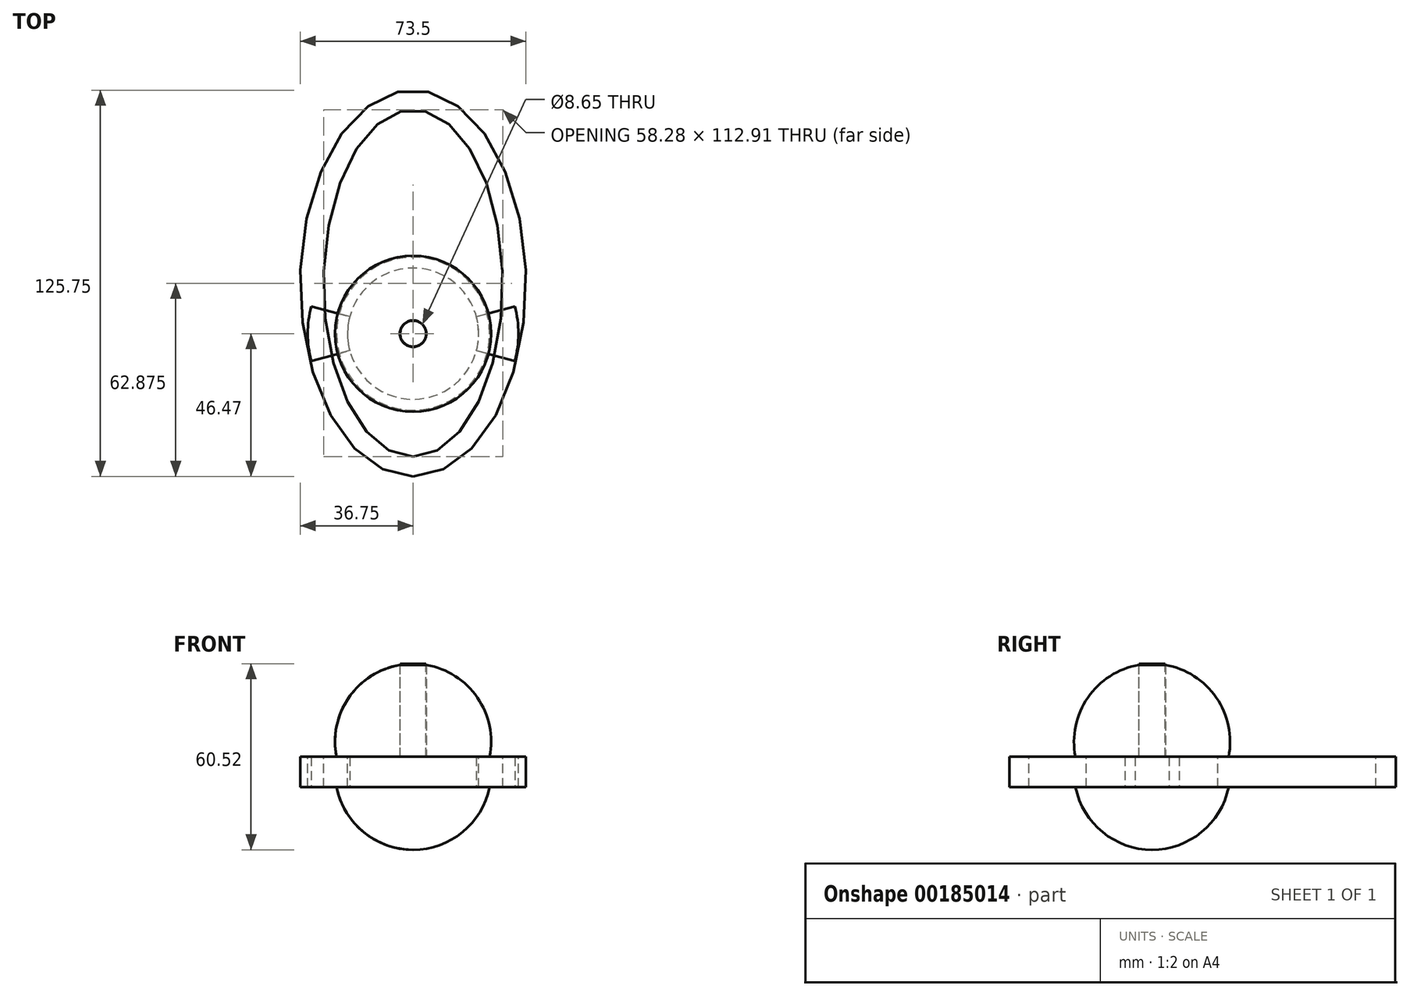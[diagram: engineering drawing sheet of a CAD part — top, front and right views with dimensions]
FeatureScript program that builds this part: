
annotation { "Feature Type Name" : "Feature", "Feature Type Description" : "" }
export const myFeature = defineFeature(function(context is Context, id is Id, definition is map)
    precondition{}
    {
        {
            var Q0;
            Q0=qCreatedBy(makeId("Front.planeOp"),FACE);
            var sketch = newSketch(context, id + "F0", { "sketchPlane" : qUnion([Q0])});
            skLineSegment(sketch, "E0", {"start": v(0, 0) * mm, "end": v(4.22, 0) * mm});
            skLineSegment(sketch, "E1", {"start": v(4.22, 0) * mm, "end": v(4.22, 30.26) * mm});
            skLineSegment(sketch, "E2", {"start": v(0, 0) * mm, "end": v(0, 7.45) * mm});
            skLineSegment(sketch, "E3", {"start": v(0, 56.49) * mm, "end": v(0, 30.26) * mm, "construction": true});
            skLineSegment(sketch, "E4", {"start": v(0, -25.4) * mm, "end": v(0, 0) * mm});
            skLineSegment(sketch, "E5", {"start": v(4.22, 30.26) * mm, "end": v(0, 30.26) * mm});
            skLineSegment(sketch, "E6", {"start": v(0, 30.26) * mm, "end": v(0, 7.45) * mm});
            skLineSegment(sketch, "E7.trimOffspring", {"start": v(0, 0) * mm, "end": v(0, -51.13) * mm, "construction": true});
            skLineSegment(sketch, "E8", {"start": v(0, 0) * mm, "end": v(21.35, 0) * mm});
            skPoint(sketch, "E8.endSnap0", {"position": v(2.1, 0) * mm});
            skLineSegment(sketch, "E9", {"start": v(21.35, 0) * mm, "end": v(21.35, -9.9) * mm});
            skLineSegment(sketch, "E10", {"start": v(21.35, -9.9) * mm, "end": v(0, -9.9) * mm});
            skSolve(sketch);
        }
        {
            var Q0;
            Q0=qCreatedBy(makeId("Front.planeOp"),FACE);
            var sketch = newSketch(context, id + "F1", { "sketchPlane" : qUnion([Q0])});
            skLineSegment(sketch, "E11", {"start": v(0, 0) * mm, "end": v(34.3, 0) * mm});
            skLineSegment(sketch, "E12", {"start": v(34.3, 0) * mm, "end": v(43.18, 0) * mm});
            skLineSegment(sketch, "E13", {"start": v(43.18, 0) * mm, "end": v(43.18, -9.9) * mm});
            skLineSegment(sketch, "E14", {"start": v(43.18, -9.9) * mm, "end": v(0, -9.9) * mm});
            skLineSegment(sketch, "E15", {"start": v(0, 0) * mm, "end": v(0, -9.9) * mm});
            skLineSegment(sketch, "E16", {"start": v(0, -9.9) * mm, "end": v(-43.18, -9.9) * mm});
            skLineSegment(sketch, "E17", {"start": v(-43.18, -9.9) * mm, "end": v(-43.18, 0) * mm});
            skLineSegment(sketch, "E18", {"start": v(-43.18, 0) * mm, "end": v(0, 0) * mm});
            skLineSegment(sketch, "E19", {"start": v(34.3, 0) * mm, "end": v(34.3, -9.9) * mm});
            skLineSegment(sketch, "E20", {"start": v(0, 0) * mm, "end": v(-34.3, 0) * mm});
            skLineSegment(sketch, "E21", {"start": v(-34.3, 0) * mm, "end": v(-34.3, -9.9) * mm});
            skLineSegment(sketch, "E22", {"start": v(0, 0) * mm, "end": v(21.35, 0) * mm});
            skLineSegment(sketch, "E23", {"start": v(0, 0) * mm, "end": v(-21.35, 0) * mm});
            skLineSegment(sketch, "E24", {"start": v(-21.35, 0) * mm, "end": v(-21.35, -9.9) * mm});
            skLineSegment(sketch, "E25", {"start": v(21.35, 0) * mm, "end": v(21.35, -9.9) * mm});
            skLineSegment(sketch, "E26", {"start": v(21.35, 0) * mm, "end": v(21.35, -1.77) * mm});
            skLineSegment(sketch, "E27", {"start": v(21.35, -9.9) * mm, "end": v(21.35, -8.12) * mm});
            skLineSegment(sketch, "E28", {"start": v(21.35, -8.12) * mm, "end": v(43.18, -8.12) * mm});
            skLineSegment(sketch, "E29", {"start": v(21.35, -1.77) * mm, "end": v(43.18, -1.77) * mm});
            skLineSegment(sketch, "E30", {"start": v(-21.35, -9.9) * mm, "end": v(-21.35, -8.12) * mm});
            skLineSegment(sketch, "E31", {"start": v(-21.35, 0) * mm, "end": v(-21.35, -1.77) * mm});
            skLineSegment(sketch, "E32", {"start": v(-21.35, -1.77) * mm, "end": v(-43.18, -1.77) * mm});
            skLineSegment(sketch, "E33", {"start": v(-21.35, -8.12) * mm, "end": v(-43.18, -8.12) * mm});
            skSolve(sketch);
        }
        {
            var Q0;
            {var subQ5=sQuery(id+"F1.wireOp",EDGE,"E24");Q0=makeQuery(id+"F1.imprint","IMPRINT",FACE,{"disambiguationData":[TD([[makeQuery(id+"F1.imprint","IMPRINT",EDGE,{"derivedFrom":subQ5}),-1.0]])]});}
            var Q1;
            {var subQ5=sQuery(id+"F1.wireOp",EDGE,"E25");Q1=makeQuery(id+"F1.imprint","IMPRINT",FACE,{"disambiguationData":[TD([[makeQuery(id+"F1.imprint","IMPRINT",EDGE,{"derivedFrom":subQ5}),1.0]])]});}
            var Q2;
            {var subQ0=sQuery(id+"F1.wireOp",EDGE,"E20");Q2=makeQuery(id+"F1.imprint","IMPRINT",FACE,{"disambiguationData":[TD([[makeQuery(id+"F1.imprint","IMPRINT",EDGE,{"derivedFrom":subQ0}),1.0]])]});}
            var Q3;
            {var subQ3=sQuery(id+"F1.wireOp",EDGE,"E30");Q3=makeQuery(id+"F1.imprint","IMPRINT",FACE,{"disambiguationData":[TD([[makeQuery(id+"F1.imprint","IMPRINT",EDGE,{"derivedFrom":subQ3}),1.0]])]});}
            var Q4;
            {var subQ3=sQuery(id+"F1.wireOp",EDGE,"E27");Q4=makeQuery(id+"F1.imprint","IMPRINT",FACE,{"disambiguationData":[TD([[makeQuery(id+"F1.imprint","IMPRINT",EDGE,{"derivedFrom":subQ3}),-1.0]])]});}
            var Q5;
            {var subQ0=sQuery(id+"F1.wireOp",EDGE,"E11");Q5=makeQuery(id+"F1.imprint","IMPRINT",FACE,{"disambiguationData":[TD([[makeQuery(id+"F1.imprint","IMPRINT",EDGE,{"derivedFrom":subQ0}),-1.0]])]});}
            var Q6;
            Q6=sQuery(id+"F0.wireOp",EDGE,"E3");
            revolve(context, id + "F2", {"entities" : qUnion([Q0, Q1, Q2, Q3, Q4, Q5]), "axis" : qUnion([Q6]), "revolveType" : RevolveType.SYMMETRIC, "angle" : 30 * degree});
        }
        {
            var Q0;
            Q0=qSketchRegion(id+"F0",true);
            var Q1;
            Q1=sQuery(id+"F0.wireOp",EDGE,"E3");
            revolve(context, id + "F3", {"entities" : qUnion([Q0]), "axis" : qUnion([Q1]), "revolveType" : RevolveType.FULL});
        }
        {
            var Q0;
            Q0=qCreatedBy(makeId("Top.planeOp"),FACE);
            var sketch = newSketch(context, id + "F4", { "sketchPlane" : qUnion([Q0])});
            skEllipse(sketch, "E34", {"center": v(0, 16.4) * mm, "majorRadius": 62.87 * mm, "minorRadius": 36.75 * mm, "majorAxis": v(0, -1)});
            skEllipse(sketch, "E35", {"center": v(0, 16.4) * mm, "majorRadius": 56.46 * mm, "minorRadius": 29.14 * mm, "majorAxis": v(0, -1)});
            skSolve(sketch);
        }
        {
            var Q0;
            Q0=qSketchRegion(id+"F4",true);
            extrude(context, id + "F5", {"entities" : qUnion([Q0]), "oppositeDirection" : true, "depth" : 9.9 * mm});
        }
        {
            var Q0;
            Q0=qCreatedBy(makeId("Front.planeOp"),FACE);
            var sketch = newSketch(context, id + "F6", { "sketchPlane" : qUnion([Q0])});
            skArc(sketch, "E36", {"start": v(24.93, 0) * mm, "mid": v(19.6, 21.01) * mm, "end": v(0, 30.26) * mm});
            skLineSegment(sketch, "E37", {"start": v(24.93, 0) * mm, "end": v(4.33, 0) * mm});
            skLineSegment(sketch, "E38", {"start": v(4.33, 29.9) * mm, "end": v(4.33, 0) * mm});
            skPoint(sketch, "E39.start.orphan", {"position": v(0, 0) * mm});
            skLineSegment(sketch, "E40", {"start": v(0, 0) * mm, "end": v(0, 30.26) * mm, "construction": true});
            skSolve(sketch);
        }
        {
            var Q0;
            Q0=qSketchRegion(id+"F6",true);
            var Q1;
            Q1=sQuery(id+"F6.wireOp",EDGE,"E40");
            revolve(context, id + "F7", {"entities" : qUnion([Q0]), "axis" : qUnion([Q1]), "revolveType" : RevolveType.FULL});
        }
        {
            var Q0;
            Q0=qCreatedBy(makeId("Front.planeOp"),FACE);
            var sketch = newSketch(context, id + "F8", { "sketchPlane" : qUnion([Q0])});
            skArc(sketch, "E41", {"start": v(0, -30.26) * mm, "mid": v(16.08, -24.52) * mm, "end": v(24.9, -9.9) * mm});
            skLineSegment(sketch, "E42", {"start": v(0, -9.9) * mm, "end": v(33.93, -9.9) * mm});
            skLineSegment(sketch, "E43", {"start": v(0, -9.9) * mm, "end": v(0, -30.26) * mm});
            skLineSegment(sketch, "E44", {"start": v(0, 0) * mm, "end": v(0, -34.04) * mm, "construction": true});
            skSolve(sketch);
        }
        {
            var Q0;
            Q0=qSketchRegion(id+"F8",true);
            var Q1;
            Q1=sQuery(id+"F8.wireOp",EDGE,"E44");
            revolve(context, id + "F9", {"entities" : qUnion([Q0]), "axis" : qUnion([Q1]), "revolveType" : RevolveType.FULL});
        }
    });
